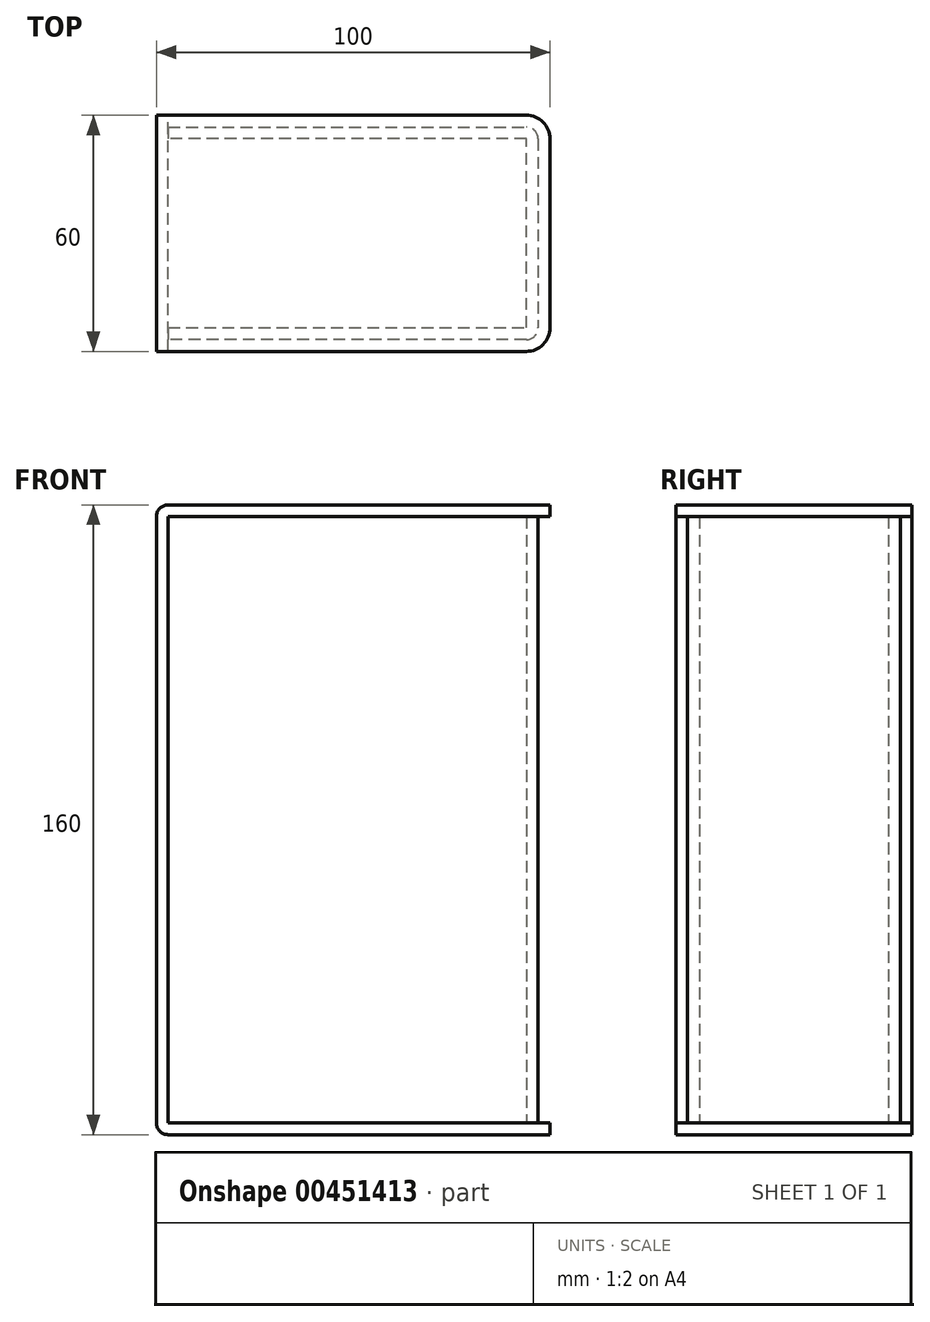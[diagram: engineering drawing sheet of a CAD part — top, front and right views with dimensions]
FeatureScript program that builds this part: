
annotation { "Feature Type Name" : "Feature", "Feature Type Description" : "" }
export const myFeature = defineFeature(function(context is Context, id is Id, definition is map)
    precondition{}
    {
        {
            var Q0;
            Q0=qCreatedBy(makeId("Front.planeOp"),FACE);
            var sketch = newSketch(context, id + "F0", { "sketchPlane" : qUnion([Q0])});
            skLineSegment(sketch, "E0", {"start": v(0, 0) * mm, "end": v(-100, 0) * mm});
            skLineSegment(sketch, "E1", {"start": v(-100, 0) * mm, "end": v(-100, 160) * mm});
            skLineSegment(sketch, "E2", {"start": v(-100, 160) * mm, "end": v(0, 160) * mm});
            skLineSegment(sketch, "E3", {"start": v(0, 160) * mm, "end": v(0, 157) * mm});
            skLineSegment(sketch, "E4", {"start": v(0, 157) * mm, "end": v(-97, 157) * mm});
            skLineSegment(sketch, "E5", {"start": v(-97, 157) * mm, "end": v(-97, 3) * mm});
            skLineSegment(sketch, "E6", {"start": v(-97, 3) * mm, "end": v(0, 3) * mm});
            skLineSegment(sketch, "E7", {"start": v(0, 3) * mm, "end": v(0, 0) * mm});
            skLineSegment(sketch, "E8", {"start": v(-97, 80) * mm, "end": v(-100, 80) * mm, "construction": true});
            skSolve(sketch);
        }
        {
            var Q0;
            Q0=makeQuery(id+"F0.imprint","IMPRINT",FACE,{"disambiguationData":[TD([[makeQuery(id+"F0.imprint","IMPRINT",EDGE,{"derivedFrom":sQuery(id+"F0.wireOp",EDGE,"E0")}),-1.0]])]});
            extrude(context, id + "F1", {"entities" : qUnion([Q0]), "endBound" : BoundingType.SYMMETRIC, "depth" : 60 * mm});
        }
        {
            var Q0;
            Q0=makeQuery(id+"F1.opExtrude","SWEPT_FACE",FACE,{"disambiguationData":[OSD([sQuery(id+"F0.wireOp",EDGE,"E6")])]});
            var sketch = newSketch(context, id + "F2", { "sketchPlane" : qUnion([Q0])});
            skLineSegment(sketch, "E9", {"start": v(-97, -27) * mm, "end": v(-3, -27) * mm});
            skLineSegment(sketch, "E10", {"start": v(-3, -27) * mm, "end": v(-3, 27) * mm});
            skLineSegment(sketch, "E11", {"start": v(-3, 27) * mm, "end": v(-97, 27) * mm});
            skLineSegment(sketch, "E12", {"start": v(-97, 27) * mm, "end": v(-97, 24) * mm});
            skLineSegment(sketch, "E13", {"start": v(-97, 24) * mm, "end": v(-6, 24) * mm});
            skLineSegment(sketch, "E14", {"start": v(-6, 24) * mm, "end": v(-6, -24) * mm});
            skLineSegment(sketch, "E15", {"start": v(-6, -24) * mm, "end": v(-97, -24) * mm});
            skLineSegment(sketch, "E16", {"start": v(-97, -24) * mm, "end": v(-97, -27) * mm});
            skLineSegment(sketch, "E17", {"start": v(-6, 0) * mm, "end": v(-3, 0) * mm, "construction": true});
            skLineSegment(sketch, "E18.MirrorCS", {"start": v(-6, 24) * mm, "end": v(-97, 24) * mm});
            skLineSegment(sketch, "E19.MirrorCS", {"start": v(-97, -24) * mm, "end": v(-6, -24) * mm});
            skLineSegment(sketch, "E20", {"start": v(-97, -27) * mm, "end": v(-97, -30) * mm, "construction": true});
            skLineSegment(sketch, "E21", {"start": v(-3, 0) * mm, "end": v(0, 0) * mm, "construction": true});
            skSolve(sketch);
        }
        {
            var Q0;
            Q0=makeQuery(id+"F2.imprint","IMPRINT",FACE,{"disambiguationData":[TD([[makeQuery(id+"F2.imprint","IMPRINT",EDGE,{"derivedFrom":sQuery(id+"F2.wireOp",EDGE,"E9")}),1.0]])]});
            var Q1;
            Q1=makeQuery(id+"F1.opExtrude","SWEPT_FACE",FACE,{"disambiguationData":[OSD([sQuery(id+"F0.wireOp",EDGE,"E4")])]});
            extrude(context, id + "F3", {"entities" : qUnion([Q0]), "endBound" : BoundingType.UP_TO_SURFACE, "endBoundEntityFace" : qUnion([Q1]), "depth" : 25 * mm});
        }
        {
            var Q0;
            Q0=makeQuery(id+"F1.opExtrude","SWEPT_EDGE",EDGE,{"disambiguationData":[OSD([sQuery(id+"F0.wireOp",EDGE,"E1"),sQuery(id+"F0.wireOp",EDGE,"E2")])]});
            var Q1;
            Q1=makeQuery(id+"F1.opExtrude","SWEPT_EDGE",EDGE,{"disambiguationData":[OSD([sQuery(id+"F0.wireOp",EDGE,"E0"),sQuery(id+"F0.wireOp",EDGE,"E1")])]});
            var Q2;
            Q2=makeQuery(id+"F3.opExtrude","SWEPT_EDGE",EDGE,{"disambiguationData":[OSD([sQuery(id+"F2.wireOp",EDGE,"E9"),sQuery(id+"F2.wireOp",EDGE,"E10")])]});
            var Q3;
            Q3=makeQuery(id+"F3.opExtrude","SWEPT_EDGE",EDGE,{"disambiguationData":[OSD([sQuery(id+"F2.wireOp",EDGE,"E10"),sQuery(id+"F2.wireOp",EDGE,"E11")])]});
            fillet(context, id + "F4", {"entities" : qUnion([Q0, Q1, Q2, Q3]), "radius" : 3 * mm, "tangentPropagation" : true, "allowEdgeOverflow" : false});
        }
        {
            var Q0;
            Q0=makeQuery(id+"F1.opExtrude","CAP_EDGE",EDGE,{"disambiguationData":[OSD([sQuery(id+"F0.wireOp",EDGE,"E3")])],"isStart":false});
            var Q1;
            Q1=makeQuery(id+"F1.opExtrude","CAP_EDGE",EDGE,{"disambiguationData":[OSD([sQuery(id+"F0.wireOp",EDGE,"E3")])],"isStart":true});
            var Q2;
            Q2=makeQuery(id+"F1.opExtrude","CAP_EDGE",EDGE,{"disambiguationData":[OSD([sQuery(id+"F0.wireOp",EDGE,"E7")])],"isStart":true});
            var Q3;
            Q3=makeQuery(id+"F1.opExtrude","CAP_EDGE",EDGE,{"disambiguationData":[OSD([sQuery(id+"F0.wireOp",EDGE,"E7")])],"isStart":false});
            fillet(context, id + "F5", {"entities" : qUnion([Q0, Q1, Q2, Q3]), "radius" : 6 * mm, "tangentPropagation" : true, "allowEdgeOverflow" : false});
        }
    });
